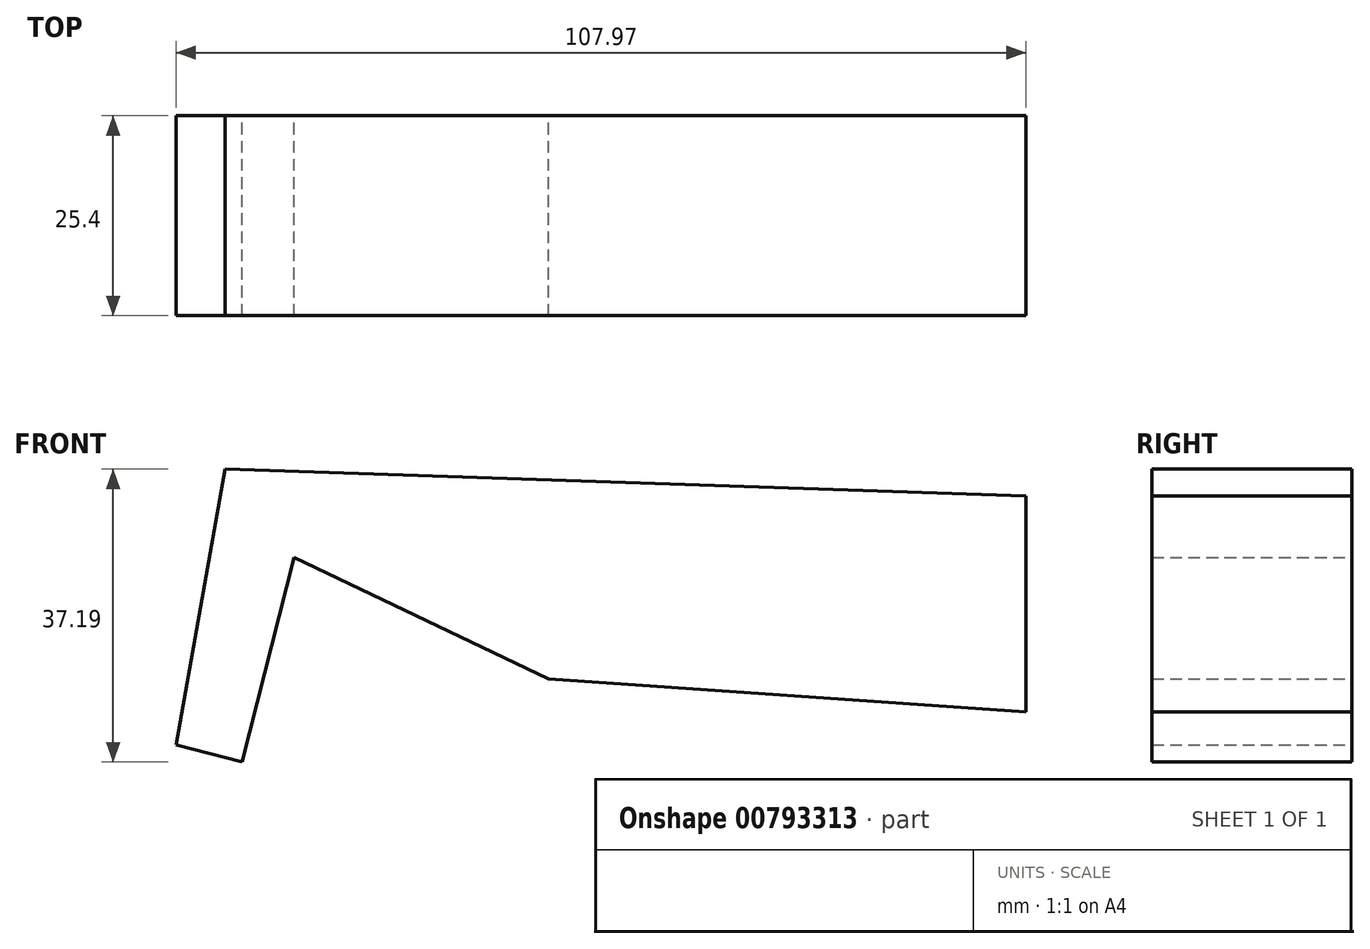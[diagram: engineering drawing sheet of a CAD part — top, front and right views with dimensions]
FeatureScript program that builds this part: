
annotation { "Feature Type Name" : "Feature", "Feature Type Description" : "" }
export const myFeature = defineFeature(function(context is Context, id is Id, definition is map)
    precondition{}
    {
        {
            var Q0;
            Q0=qCreatedBy(makeId("Front.planeOp"),FACE);
            var sketch = newSketch(context, id + "F0", { "sketchPlane" : qUnion([Q0])});
            skLineSegment(sketch, "E0", {"start": v(-63.5, 41.96) * mm, "end": v(38.3, 38.54) * mm});
            skLineSegment(sketch, "E1", {"start": v(38.3, 38.54) * mm, "end": v(38.3, 11.13) * mm});
            skLineSegment(sketch, "E2", {"start": v(38.3, 11.13) * mm, "end": v(-22.39, 15.3) * mm});
            skLineSegment(sketch, "E3", {"start": v(-22.39, 15.3) * mm, "end": v(-54.69, 30.7) * mm});
            skLineSegment(sketch, "E4", {"start": v(-54.69, 30.7) * mm, "end": v(-61.3, 4.77) * mm});
            skLineSegment(sketch, "E5", {"start": v(-61.3, 4.77) * mm, "end": v(-69.68, 6.9) * mm});
            skLineSegment(sketch, "E6", {"start": v(-69.68, 6.9) * mm, "end": v(-63.5, 41.96) * mm});
            skSolve(sketch);
        }
        {
            var Q0;
            Q0=makeQuery(id+"F0.imprint","IMPRINT",FACE,{"disambiguationData":[TD([[makeQuery(id+"F0.imprint","IMPRINT",EDGE,{"derivedFrom":sQuery(id+"F0.wireOp",EDGE,"E0")}),-1.0]])]});
            extrude(context, id + "F1", {"entities" : qUnion([Q0]), "depth" : 25.4 * mm, "offsetDistance" : 25.4 * mm});
        }
    });
